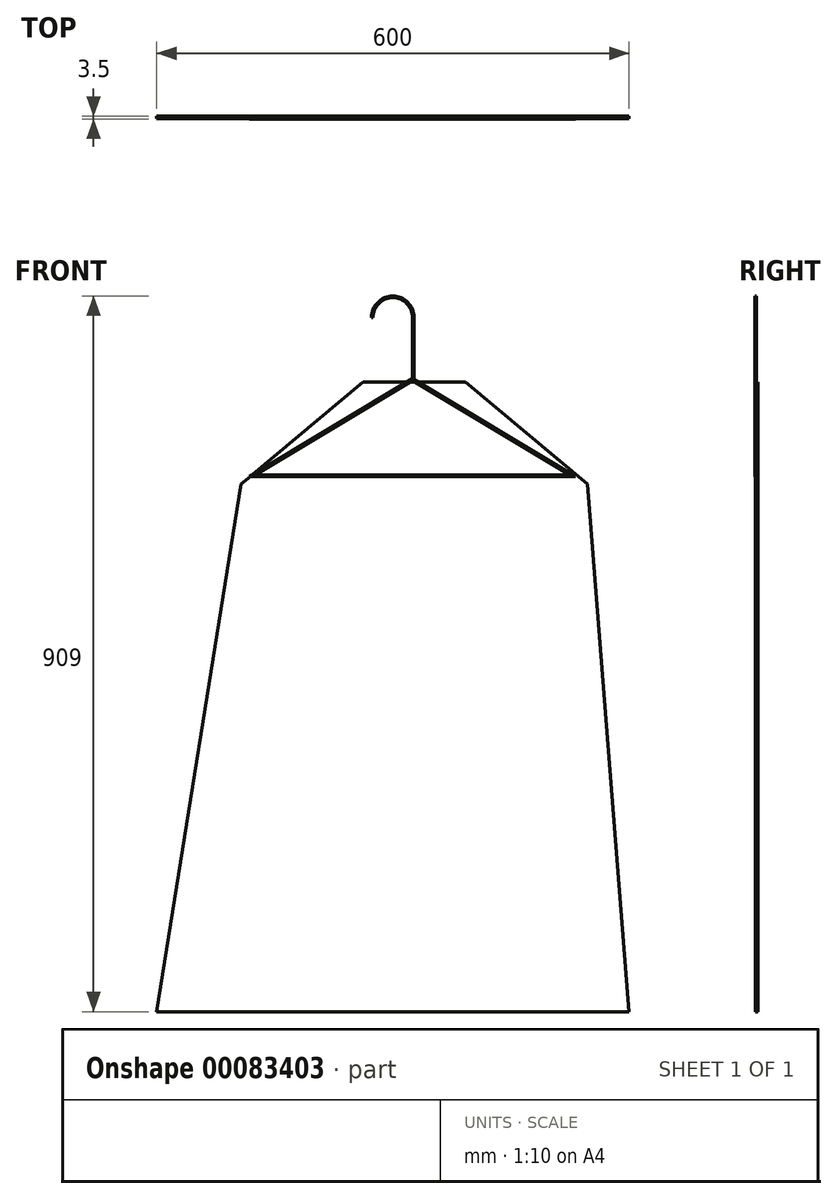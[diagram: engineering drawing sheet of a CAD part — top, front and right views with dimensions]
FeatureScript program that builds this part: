
annotation { "Feature Type Name" : "Feature", "Feature Type Description" : "" }
export const myFeature = defineFeature(function(context is Context, id is Id, definition is map)
    precondition{}
    {
        {
            var Q0;
            Q0=qCreatedBy(makeId("Front.planeOp"),FACE);
            var sketch = newSketch(context, id + "F0", { "sketchPlane" : qUnion([Q0])});
            skArc(sketch, "E0", {"start": v(-25, 0) * mm, "mid": v(0, 25) * mm, "end": v(25, 0) * mm});
            skLineSegment(sketch, "E1", {"start": v(25, 0) * mm, "end": v(25, -80) * mm});
            skLineSegment(sketch, "E2", {"start": v(25, -80) * mm, "end": v(225, -200) * mm});
            skLineSegment(sketch, "E3", {"start": v(225, -200) * mm, "end": v(-175, -200) * mm});
            skLineSegment(sketch, "E4", {"start": v(-175, -200) * mm, "end": v(25, -80) * mm});
            skLineSegment(sketch, "E5.0", {"start": v(27, 0) * mm, "end": v(27, -80) * mm});
            skArc(sketch, "E5.1", {"start": v(-27, 0) * mm, "mid": v(0, 27) * mm, "end": v(27, 0) * mm});
            skLineSegment(sketch, "E6.0", {"start": v(-182.22, -202) * mm, "end": v(25, -77.67) * mm});
            skLineSegment(sketch, "E6.1", {"start": v(232.22, -202) * mm, "end": v(-182.22, -202) * mm});
            skLineSegment(sketch, "E6.2", {"start": v(25, -77.67) * mm, "end": v(232.22, -202) * mm});
            skLineSegment(sketch, "E7", {"start": v(-25, 0) * mm, "end": v(-27, 0) * mm});
            skSolve(sketch);
        }
        {
            var Q0;
            Q0 = qSketchRegion(id + "F0", true);
            extrude(context, id + "F1", {"entities" : qUnion([Q0]), "depth" : 2 * mm});
        }
        {
            var Q0;
            Q0=qCreatedBy(makeId("Front.planeOp"),FACE);
            var sketch = newSketch(context, id + "F2", { "sketchPlane" : qUnion([Q0])});
            skLineSegment(sketch, "E8", {"start": v(-38, -82) * mm, "end": v(92, -82) * mm});
            skLineSegment(sketch, "E9", {"start": v(92, -82) * mm, "end": v(247, -212) * mm});
            skLineSegment(sketch, "E10", {"start": v(247, -212) * mm, "end": v(300, -882) * mm});
            skLineSegment(sketch, "E11", {"start": v(300, -882) * mm, "end": v(-300, -882) * mm});
            skLineSegment(sketch, "E12", {"start": v(-300, -882) * mm, "end": v(-193, -212) * mm});
            skLineSegment(sketch, "E13", {"start": v(-193, -212) * mm, "end": v(-38, -82) * mm});
            skLineSegment(sketch, "E14", {"start": v(-193, -212) * mm, "end": v(247, -212) * mm, "construction": true});
            skLineSegment(sketch, "E15", {"start": v(0, -882) * mm, "end": v(0, -212) * mm, "construction": true});
            skSolve(sketch);
        }
        {
            var Q0;
            Q0=makeQuery(id+"F2.imprint","IMPRINT",FACE,{"disambiguationData":[TD([[makeQuery(id+"F2.imprint","IMPRINT",EDGE,{"derivedFrom":sQuery(id+"F2.wireOp",EDGE,"E8")}),-1.0]])]});
            extrude(context, id + "F3", {"entities" : qUnion([Q0]), "operationType" : NewBodyOperationType.ADD, "endBound" : BoundingType.SYMMETRIC, "depth" : 3 * mm});
        }
    });
